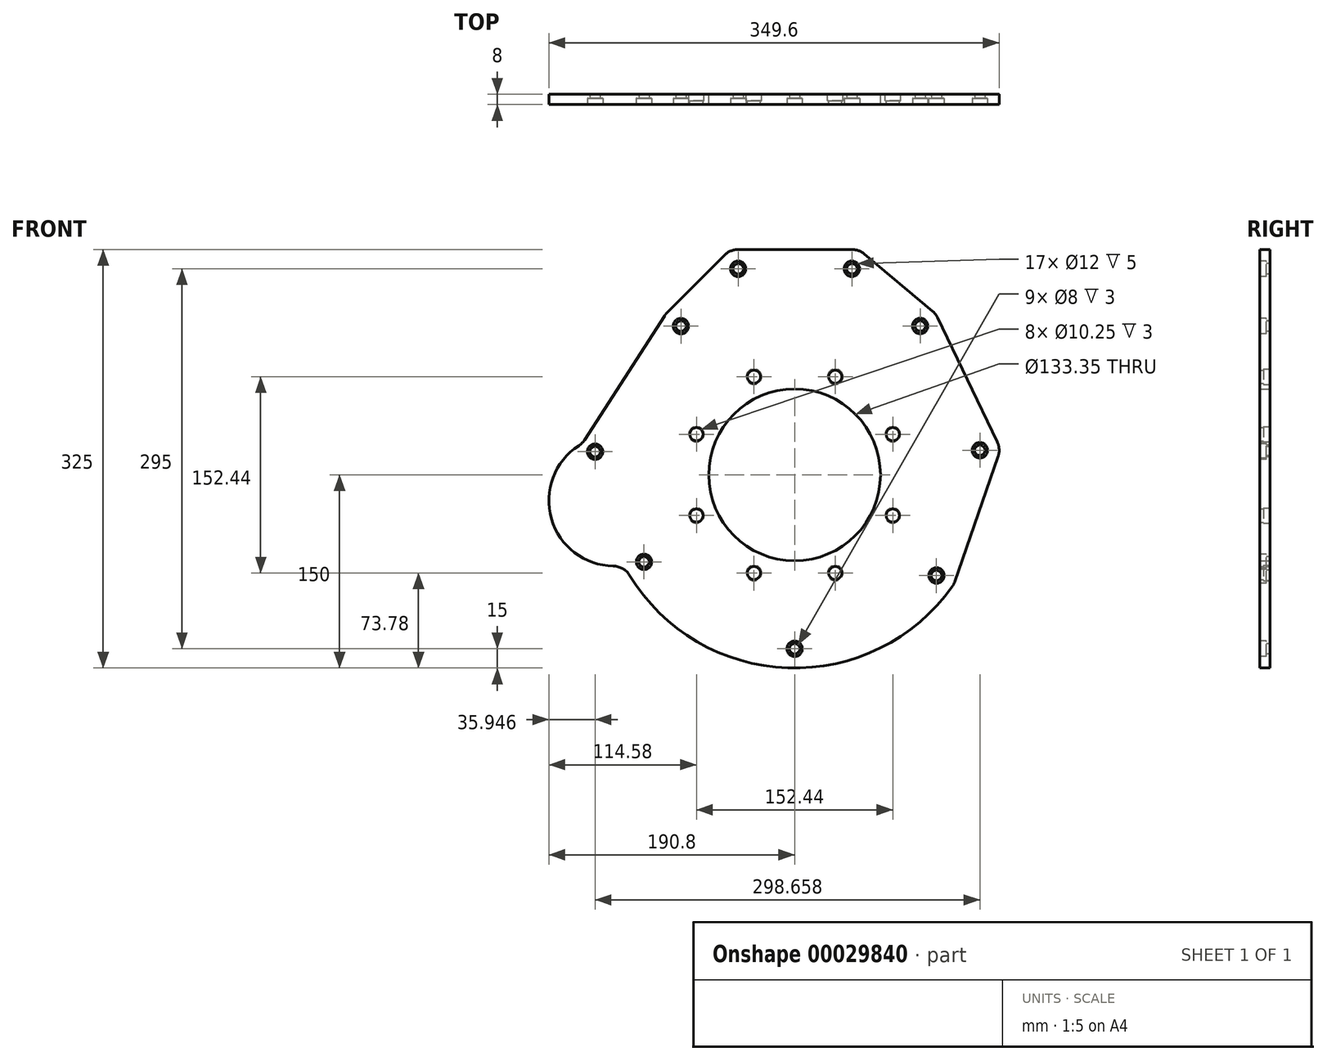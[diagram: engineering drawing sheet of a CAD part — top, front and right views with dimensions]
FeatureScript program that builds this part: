
annotation { "Feature Type Name" : "Feature", "Feature Type Description" : "" }
export const myFeature = defineFeature(function(context is Context, id is Id, definition is map)
    precondition{}
    {
        {
            var Q0;
            Q0=qCreatedBy(makeId("Front.planeOp"),FACE);
            var sketch = newSketch(context, id + "F0", { "sketchPlane" : qUnion([Q0])});
            skLineSegment(sketch, "E0", {"start": v(-50, 175) * mm, "end": v(50, 175) * mm});
            skLineSegment(sketch, "E1", {"start": v(50, 175) * mm, "end": v(109.59, 125) * mm});
            skLineSegment(sketch, "E2", {"start": v(109.59, 125) * mm, "end": v(160, 20) * mm});
            skLineSegment(sketch, "E3", {"start": v(-165, 24.22) * mm, "end": v(-100, 125) * mm});
            skLineSegment(sketch, "E4", {"start": v(-100, 125) * mm, "end": v(-50, 175) * mm});
            skLineSegment(sketch, "E5", {"start": v(0, 175) * mm, "end": v(0, 0) * mm, "construction": true});
            skArc(sketch, "E6", {"start": v(-165, 24.22) * mm, "mid": v(-188.04, -36.51) * mm, "end": v(-132.53, -70.25) * mm});
            skArc(sketch, "E7", {"start": v(-132.53, -70.25) * mm, "mid": v(-8.63, -149.75) * mm, "end": v(123.6, -85) * mm});
            skLineSegment(sketch, "E8", {"start": v(160, 20) * mm, "end": v(123.6, -85) * mm});
            skCircle(sketch, "E9", {"center": v(0, 0) * mm, "radius": 66.68 * mm});
            skSolve(sketch);
        }
        {
            var Q0;
            Q0 = qSketchRegion(id + "F0", true);
            extrude(context, id + "F1", {"entities" : qUnion([Q0]), "depth" : 8 * mm});
        }
        {
            var Q0;
            Q0=makeQuery(id+"F1.opExtrude","CAP_FACE",FACE,{"disambiguationData":[OSD([sQuery(id+"F0.wireOp",EDGE,"E0"),sQuery(id+"F0.wireOp",EDGE,"E1"),sQuery(id+"F0.wireOp",EDGE,"E2"),sQuery(id+"F0.wireOp",EDGE,"E3"),sQuery(id+"F0.wireOp",EDGE,"E4"),sQuery(id+"F0.wireOp",EDGE,"E6"),sQuery(id+"F0.wireOp",EDGE,"E7"),sQuery(id+"F0.wireOp",EDGE,"E8"),sQuery(id+"F0.wireOp",EDGE,"E9")])],"isStart":true});
            var sketch = newSketch(context, id + "F2", { "sketchPlane" : qUnion([Q0])});
            skCircle(sketch, "E10", {"center": v(0, 0) * mm, "radius": 82.5 * mm, "construction": true});
            skCircle(sketch, "E11", {"center": v(-31.57, 76.22) * mm, "radius": 5.12 * mm});
            skCircle(sketch, "E12.1.0", {"center": v(-76.22, 31.57) * mm, "radius": 5.12 * mm});
            skCircle(sketch, "E12.2.0", {"center": v(-76.22, -31.57) * mm, "radius": 5.12 * mm});
            skCircle(sketch, "E12.3.0", {"center": v(-31.57, -76.22) * mm, "radius": 5.12 * mm});
            skCircle(sketch, "E12.4.0", {"center": v(31.57, -76.22) * mm, "radius": 5.12 * mm});
            skCircle(sketch, "E12.5.0", {"center": v(76.22, -31.57) * mm, "radius": 5.12 * mm});
            skCircle(sketch, "E12.6.0", {"center": v(76.22, 31.57) * mm, "radius": 5.12 * mm});
            skCircle(sketch, "E12.7.0", {"center": v(31.57, 76.22) * mm, "radius": 5.12 * mm});
            skLineSegment(sketch, "E13", {"start": v(-31.57, 76.22) * mm, "end": v(0, 0) * mm, "construction": true});
            skLineSegment(sketch, "E14", {"start": v(0, 0) * mm, "end": v(0, 82.5) * mm, "construction": true});
            skSolve(sketch);
        }
        {
            var Q0;
            Q0=sQuery(id+"F2.wireOp",VERTEX,"E11.center");
            var Q1;
            Q1=sQuery(id+"F2.wireOp",VERTEX,"E12.7.0.center");
            var Q2;
            Q2=sQuery(id+"F2.wireOp",VERTEX,"E12.6.0.center");
            var Q3;
            Q3=sQuery(id+"F2.wireOp",VERTEX,"E12.5.0.center");
            var Q4;
            Q4=sQuery(id+"F2.wireOp",VERTEX,"E12.4.0.center");
            var Q5;
            Q5=sQuery(id+"F2.wireOp",VERTEX,"E12.3.0.center");
            var Q6;
            Q6=sQuery(id+"F2.wireOp",VERTEX,"E12.2.0.center");
            var Q7;
            Q7=sQuery(id+"F2.wireOp",VERTEX,"E12.1.0.center");
            var Q8;
            Q8=makeQuery(id+"F1.opExtrude","SWEPT_BODY",BODY,{"disambiguationData":[OSD([sQuery(id+"F0.wireOp",EDGE,"E0"),sQuery(id+"F0.wireOp",EDGE,"E1"),sQuery(id+"F0.wireOp",EDGE,"E2"),sQuery(id+"F0.wireOp",EDGE,"E3"),sQuery(id+"F0.wireOp",EDGE,"E4"),sQuery(id+"F0.wireOp",EDGE,"E6"),sQuery(id+"F0.wireOp",EDGE,"E7"),sQuery(id+"F0.wireOp",EDGE,"E8"),sQuery(id+"F0.wireOp",EDGE,"E9")])]});
            hole(context, id + "F3", {"style" : HoleStyle.C_BORE, "holeDiameter" : 8 * mm, "cBoreDiameter" : 12 * mm, "cBoreDepth" : 5 * mm, "endStyle" : HoleEndStyle.THROUGH, "locations" : qUnion([Q0, Q1, Q2, Q3, Q4, Q5, Q6, Q7]), "scope" : qUnion([Q8])});
        }
        {
            var Q0;
            Q0=makeQuery(id+"F1.opExtrude","SWEPT_EDGE",EDGE,{"disambiguationData":[OSD([sQuery(id+"F0.wireOp",EDGE,"E2"),sQuery(id+"F0.wireOp",EDGE,"E8")])]});
            var Q1;
            Q1=makeQuery(id+"F1.opExtrude","SWEPT_EDGE",EDGE,{"disambiguationData":[OSD([sQuery(id+"F0.wireOp",EDGE,"E1"),sQuery(id+"F0.wireOp",EDGE,"E2")])]});
            var Q2;
            Q2=makeQuery(id+"F1.opExtrude","SWEPT_EDGE",EDGE,{"disambiguationData":[OSD([sQuery(id+"F0.wireOp",EDGE,"E0"),sQuery(id+"F0.wireOp",EDGE,"E1")])]});
            var Q3;
            Q3=makeQuery(id+"F1.opExtrude","SWEPT_EDGE",EDGE,{"disambiguationData":[OSD([sQuery(id+"F0.wireOp",EDGE,"E0"),sQuery(id+"F0.wireOp",EDGE,"E4")])]});
            var Q4;
            Q4=makeQuery(id+"F1.opExtrude","SWEPT_EDGE",EDGE,{"disambiguationData":[OSD([sQuery(id+"F0.wireOp",EDGE,"E3"),sQuery(id+"F0.wireOp",EDGE,"E4")])]});
            var Q5;
            Q5=makeQuery(id+"F1.opExtrude","SWEPT_EDGE",EDGE,{"disambiguationData":[OSD([sQuery(id+"F0.wireOp",EDGE,"E3"),sQuery(id+"F0.wireOp",EDGE,"E6")])]});
            var Q6;
            Q6=makeQuery(id+"F1.opExtrude","SWEPT_EDGE",EDGE,{"disambiguationData":[OSD([sQuery(id+"F0.wireOp",EDGE,"E6"),sQuery(id+"F0.wireOp",EDGE,"E7")])]});
            var Q7;
            Q7=makeQuery(id+"F1.opExtrude","SWEPT_EDGE",EDGE,{"disambiguationData":[OSD([sQuery(id+"F0.wireOp",EDGE,"E7"),sQuery(id+"F0.wireOp",EDGE,"E8")])]});
            fillet(context, id + "F4", {"entities" : qUnion([Q0, Q1, Q2, Q3, Q4, Q5, Q6, Q7]), "radius" : 15 * mm, "tangentPropagation" : true, "allowEdgeOverflow" : false});
        }
        {
            var Q0;
            Q0=makeQuery(id+"F1.opExtrude","CAP_FACE",FACE,{"disambiguationData":[OSD([sQuery(id+"F0.wireOp",EDGE,"E0"),sQuery(id+"F0.wireOp",EDGE,"E1"),sQuery(id+"F0.wireOp",EDGE,"E2"),sQuery(id+"F0.wireOp",EDGE,"E3"),sQuery(id+"F0.wireOp",EDGE,"E4"),sQuery(id+"F0.wireOp",EDGE,"E6"),sQuery(id+"F0.wireOp",EDGE,"E7"),sQuery(id+"F0.wireOp",EDGE,"E8"),sQuery(id+"F0.wireOp",EDGE,"E9")])],"isStart":false});
            var sketch = newSketch(context, id + "F5", { "sketchPlane" : qUnion([Q0])});
            skPoint(sketch, "E15", {"position": v(-43.79, 160) * mm});
            skPoint(sketch, "E16", {"position": v(44.54, 160) * mm});
            skPoint(sketch, "E17", {"position": v(97.47, 115.59) * mm});
            skPoint(sketch, "E18", {"position": v(143.8, 19.08) * mm});
            skPoint(sketch, "E19", {"position": v(110.1, -78.12) * mm});
            skPoint(sketch, "E20", {"position": v(0, -135) * mm});
            skPoint(sketch, "E21", {"position": v(-116.91, -67.5) * mm});
            skPoint(sketch, "E22", {"position": v(-154.85, 18) * mm});
            skPoint(sketch, "E23", {"position": v(-88.26, 115.52) * mm});
            skCircle(sketch, "E24", {"center": v(0, 0) * mm, "radius": 135 * mm, "construction": true});
            skLineSegment(sketch, "E25", {"start": v(0, 0) * mm, "end": v(-116.91, -67.5) * mm, "construction": true});
            skLineSegment(sketch, "E26", {"start": v(0, 0) * mm, "end": v(0, -135) * mm, "construction": true});
            skCircle(sketch, "E27", {"center": v(-140, -20) * mm, "radius": 40.8 * mm, "construction": true});
            skSolve(sketch);
        }
        {
            var Q0;
            Q0=sQuery(id+"F5.wireOp",VERTEX,"E15");
            var Q1;
            Q1=sQuery(id+"F5.wireOp",VERTEX,"E23");
            var Q2;
            Q2=sQuery(id+"F5.wireOp",VERTEX,"E22");
            var Q3;
            Q3=sQuery(id+"F5.wireOp",VERTEX,"E21");
            var Q4;
            Q4=sQuery(id+"F5.wireOp",VERTEX,"E20");
            var Q5;
            Q5=sQuery(id+"F5.wireOp",VERTEX,"E19");
            var Q6;
            Q6=sQuery(id+"F5.wireOp",VERTEX,"E18");
            var Q7;
            Q7=sQuery(id+"F5.wireOp",VERTEX,"E17");
            var Q8;
            Q8=sQuery(id+"F5.wireOp",VERTEX,"E16");
            var Q9;
            Q9=makeQuery(id+"F1.opExtrude","SWEPT_BODY",BODY,{"disambiguationData":[OSD([sQuery(id+"F0.wireOp",EDGE,"E0"),sQuery(id+"F0.wireOp",EDGE,"E1"),sQuery(id+"F0.wireOp",EDGE,"E2"),sQuery(id+"F0.wireOp",EDGE,"E3"),sQuery(id+"F0.wireOp",EDGE,"E4"),sQuery(id+"F0.wireOp",EDGE,"E6"),sQuery(id+"F0.wireOp",EDGE,"E7"),sQuery(id+"F0.wireOp",EDGE,"E8"),sQuery(id+"F0.wireOp",EDGE,"E9")])]});
            hole(context, id + "F6", {"style" : HoleStyle.C_BORE, "holeDiameter" : 8 * mm, "cBoreDiameter" : 12 * mm, "cBoreDepth" : 5 * mm, "endStyle" : HoleEndStyle.THROUGH, "locations" : qUnion([Q0, Q1, Q2, Q3, Q4, Q5, Q6, Q7, Q8]), "scope" : qUnion([Q9])});
        }
        {
            var Q0;
            Q0 = qSketchRegion(id + "F2", true);
            extrude(context, id + "F7", {"entities" : qUnion([Q0]), "operationType" : NewBodyOperationType.REMOVE, "endBound" : BoundingType.THROUGH_ALL, "oppositeDirection" : true, "depth" : 25 * mm});
        }
    });
